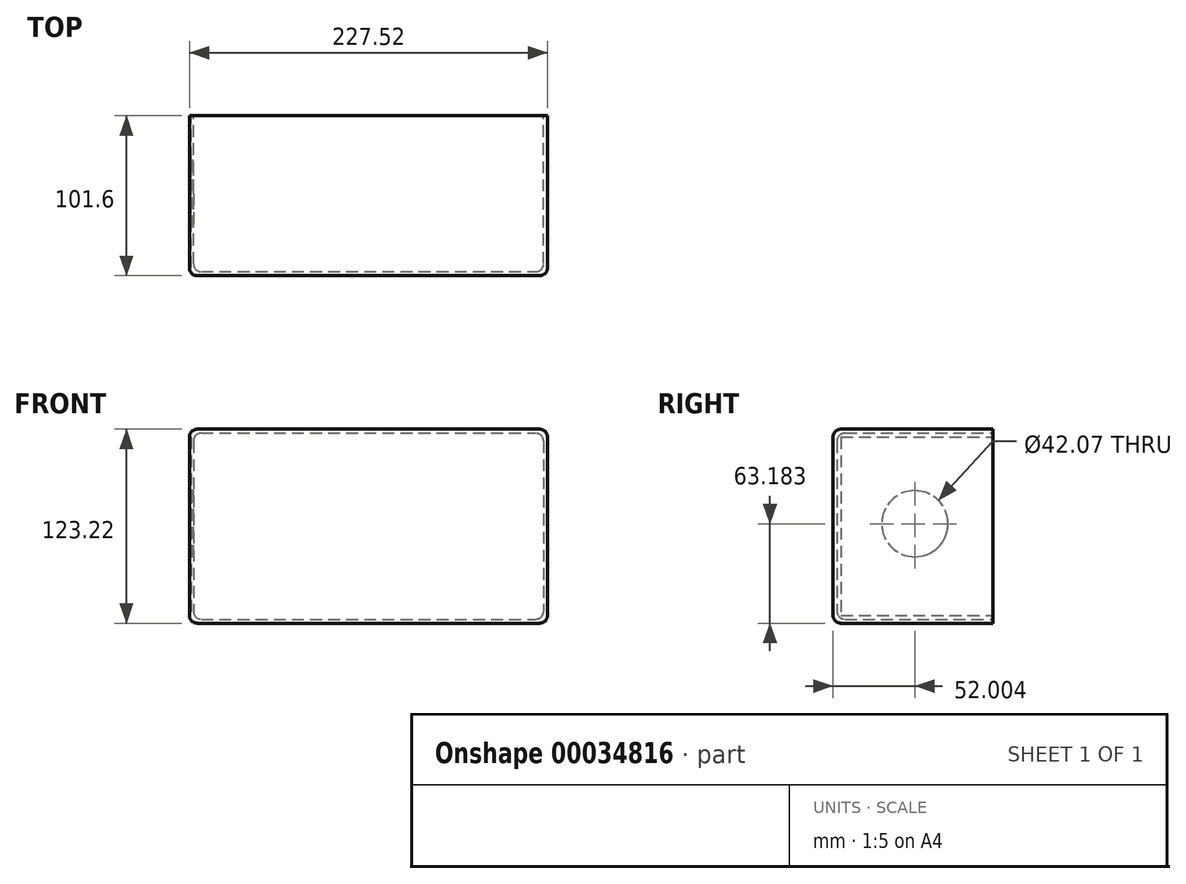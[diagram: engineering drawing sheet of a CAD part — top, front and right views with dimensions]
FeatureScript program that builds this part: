
annotation { "Feature Type Name" : "Feature", "Feature Type Description" : "" }
export const myFeature = defineFeature(function(context is Context, id is Id, definition is map)
    precondition{}
    {
        {
            var Q0;
            Q0=qCreatedBy(makeId("Front.planeOp"),FACE);
            var sketch = newSketch(context, id + "F0", { "sketchPlane" : qUnion([Q0])});
            skLineSegment(sketch, "E0.bottom", {"start": v(-59.65, 66.94) * mm, "end": v(167.87, 66.94) * mm});
            skLineSegment(sketch, "E0.top", {"start": v(-59.65, -56.28) * mm, "end": v(167.87, -56.28) * mm});
            skLineSegment(sketch, "E0.left", {"start": v(-59.65, 66.94) * mm, "end": v(-59.65, -56.28) * mm});
            skLineSegment(sketch, "E0.right", {"start": v(167.87, 66.94) * mm, "end": v(167.87, -56.28) * mm});
            skSolve(sketch);
        }
        {
            var Q0;
            Q0=makeQuery(id+"F0.imprint","IMPRINT",FACE,{"disambiguationData":[TD([[makeQuery(id+"F0.imprint","IMPRINT",EDGE,{"derivedFrom":sQuery(id+"F0.wireOp",EDGE,"E0.bottom")}),-1.0]])]});
            extrude(context, id + "F1", {"entities" : qUnion([Q0]), "depth" : 101.6 * mm});
        }
        {
            var Q0;
            Q0=makeQuery(id+"F1.opExtrude","CAP_FACE",FACE,{"disambiguationData":[OSD([sQuery(id+"F0.wireOp",EDGE,"E0.bottom"),sQuery(id+"F0.wireOp",EDGE,"E0.top"),sQuery(id+"F0.wireOp",EDGE,"E0.left"),sQuery(id+"F0.wireOp",EDGE,"E0.right")])],"isStart":true});
            shell(context, id + "F2", {"entities" : qUnion([Q0]), "thickness" : 2.54 * mm});
        }
        {
            var Q0;
            {var subQ0=sQuery(id+"F0.wireOp",EDGE,"E0.bottom");Q0=makeQuery(id+"F2.opShell","OFFSET_EDGE",EDGE,{"disambiguationData":[OSD([subQ0]),TDD([makeQuery(id+"F1.opExtrude","CAP_EDGE",EDGE,{"disambiguationData":[OSD([subQ0])],"isStart":false})])]});}
            fillet(context, id + "F3", {"entities" : qUnion([Q0]), "radius" : 5.08 * mm, "tangentPropagation" : true, "allowEdgeOverflow" : false});
        }
        {
            var Q0;
            {var subQ0=sQuery(id+"F0.wireOp",EDGE,"E0.left");Q0=makeQuery(id+"F2.opShell","OFFSET_EDGE",EDGE,{"disambiguationData":[OSD([subQ0]),TDD([makeQuery(id+"F1.opExtrude","CAP_EDGE",EDGE,{"disambiguationData":[OSD([subQ0])],"isStart":false})])]});}
            fillet(context, id + "F4", {"entities" : qUnion([Q0]), "radius" : 5.08 * mm, "tangentPropagation" : true, "allowEdgeOverflow" : false});
        }
        {
            var Q0;
            {var subQ0=sQuery(id+"F0.wireOp",EDGE,"E0.top");Q0=makeQuery(id+"F2.opShell","OFFSET_EDGE",EDGE,{"disambiguationData":[OSD([subQ0]),TDD([makeQuery(id+"F1.opExtrude","CAP_EDGE",EDGE,{"disambiguationData":[OSD([subQ0])],"isStart":false})])]});}
            fillet(context, id + "F5", {"entities" : qUnion([Q0]), "radius" : 5.08 * mm, "tangentPropagation" : true, "allowEdgeOverflow" : false});
        }
        {
            var Q0;
            {var subQ0=sQuery(id+"F0.wireOp",EDGE,"E0.right");Q0=makeQuery(id+"F2.opShell","OFFSET_EDGE",EDGE,{"disambiguationData":[OSD([subQ0]),TDD([makeQuery(id+"F1.opExtrude","CAP_EDGE",EDGE,{"disambiguationData":[OSD([subQ0])],"isStart":false})])]});}
            fillet(context, id + "F6", {"entities" : qUnion([Q0]), "radius" : 5.08 * mm, "tangentPropagation" : true, "allowEdgeOverflow" : false});
        }
        {
            var Q0;
            Q0=makeQuery(id+"F1.opExtrude","SWEPT_EDGE",EDGE,{"disambiguationData":[OSD([sQuery(id+"F0.wireOp",EDGE,"E0.bottom"),sQuery(id+"F0.wireOp",EDGE,"E0.left")])]});
            fillet(context, id + "F7", {"entities" : qUnion([Q0]), "radius" : 5.08 * mm, "tangentPropagation" : true, "allowEdgeOverflow" : false});
        }
        {
            var Q0;
            Q0=makeQuery(id+"F1.opExtrude","SWEPT_EDGE",EDGE,{"disambiguationData":[OSD([sQuery(id+"F0.wireOp",EDGE,"E0.top"),sQuery(id+"F0.wireOp",EDGE,"E0.left")])]});
            fillet(context, id + "F8", {"entities" : qUnion([Q0]), "radius" : 5.08 * mm, "tangentPropagation" : true, "allowEdgeOverflow" : false});
        }
        {
            var Q0;
            Q0=makeQuery(id+"F1.opExtrude","SWEPT_EDGE",EDGE,{"disambiguationData":[OSD([sQuery(id+"F0.wireOp",EDGE,"E0.bottom"),sQuery(id+"F0.wireOp",EDGE,"E0.right")])]});
            fillet(context, id + "F9", {"entities" : qUnion([Q0]), "radius" : 5.08 * mm, "tangentPropagation" : true, "allowEdgeOverflow" : false});
        }
        {
            var Q0;
            {var subQ0=sQuery(id+"F0.wireOp",EDGE,"E0.bottom");Q0=makeQuery(id+"F9.opFillet","BLEND_EDGE",EDGE,{"blendedFrom":[makeQuery(id+"F1.opExtrude","SWEPT_EDGE",EDGE,{"disambiguationData":[OSD([subQ0,sQuery(id+"F0.wireOp",EDGE,"E0.right")])]}),makeQuery(id+"F1.opExtrude","SWEPT_FACE",FACE,{"disambiguationData":[OSD([subQ0])]})],"blendedInto":[makeQuery(id+"F1.opExtrude","SWEPT_FACE",FACE,{"disambiguationData":[OSD([subQ0])]})]});}
            var Q1;
            Q1=makeQuery(id+"F1.opExtrude","SWEPT_EDGE",EDGE,{"disambiguationData":[OSD([sQuery(id+"F0.wireOp",EDGE,"E0.top"),sQuery(id+"F0.wireOp",EDGE,"E0.right")])]});
            fillet(context, id + "F10", {"entities" : qUnion([Q0, Q1]), "radius" : 5.08 * mm, "tangentPropagation" : true, "allowEdgeOverflow" : false});
        }
        {
            var Q0;
            Q0=makeQuery(id+"F1.opExtrude","CAP_EDGE",EDGE,{"disambiguationData":[OSD([sQuery(id+"F0.wireOp",EDGE,"E0.bottom")])],"isStart":false});
            fillet(context, id + "F11", {"entities" : qUnion([Q0]), "radius" : 5.08 * mm, "tangentPropagation" : true, "allowEdgeOverflow" : false});
        }
        {
            var Q0;
            Q0=makeQuery(id+"F1.opExtrude","SWEPT_FACE",FACE,{"disambiguationData":[OSD([sQuery(id+"F0.wireOp",EDGE,"E0.left")])]});
            var sketch = newSketch(context, id + "F12", { "sketchPlane" : qUnion([Q0])});
            skCircle(sketch, "E1", {"center": v(49.6, 6.9) * mm, "radius": 21.03 * mm});
            skSolve(sketch);
        }
        {
            var Q0;
            Q0=makeQuery(id+"F12.imprint","IMPRINT",FACE,{"disambiguationData":[TD([[makeQuery(id+"F12.imprint","IMPRINT",EDGE,{"derivedFrom":sQuery(id+"F12.wireOp",EDGE,"E1")}),-1.0]])]});
            extrude(context, id + "F13", {"entities" : qUnion([Q0]), "operationType" : NewBodyOperationType.REMOVE, "oppositeDirection" : true, "depth" : 1.07 * mm});
        }
        {
            var Q0;
            Q0=makeQuery(id+"F1.opExtrude","SWEPT_FACE",FACE,{"disambiguationData":[OSD([sQuery(id+"F0.wireOp",EDGE,"E0.left")])]});
            extrude(context, id + "F14", {"entities" : qUnion([Q0]), "operationType" : NewBodyOperationType.REMOVE, "oppositeDirection" : true, "depth" : 25.4 * mm});
        }
    });
